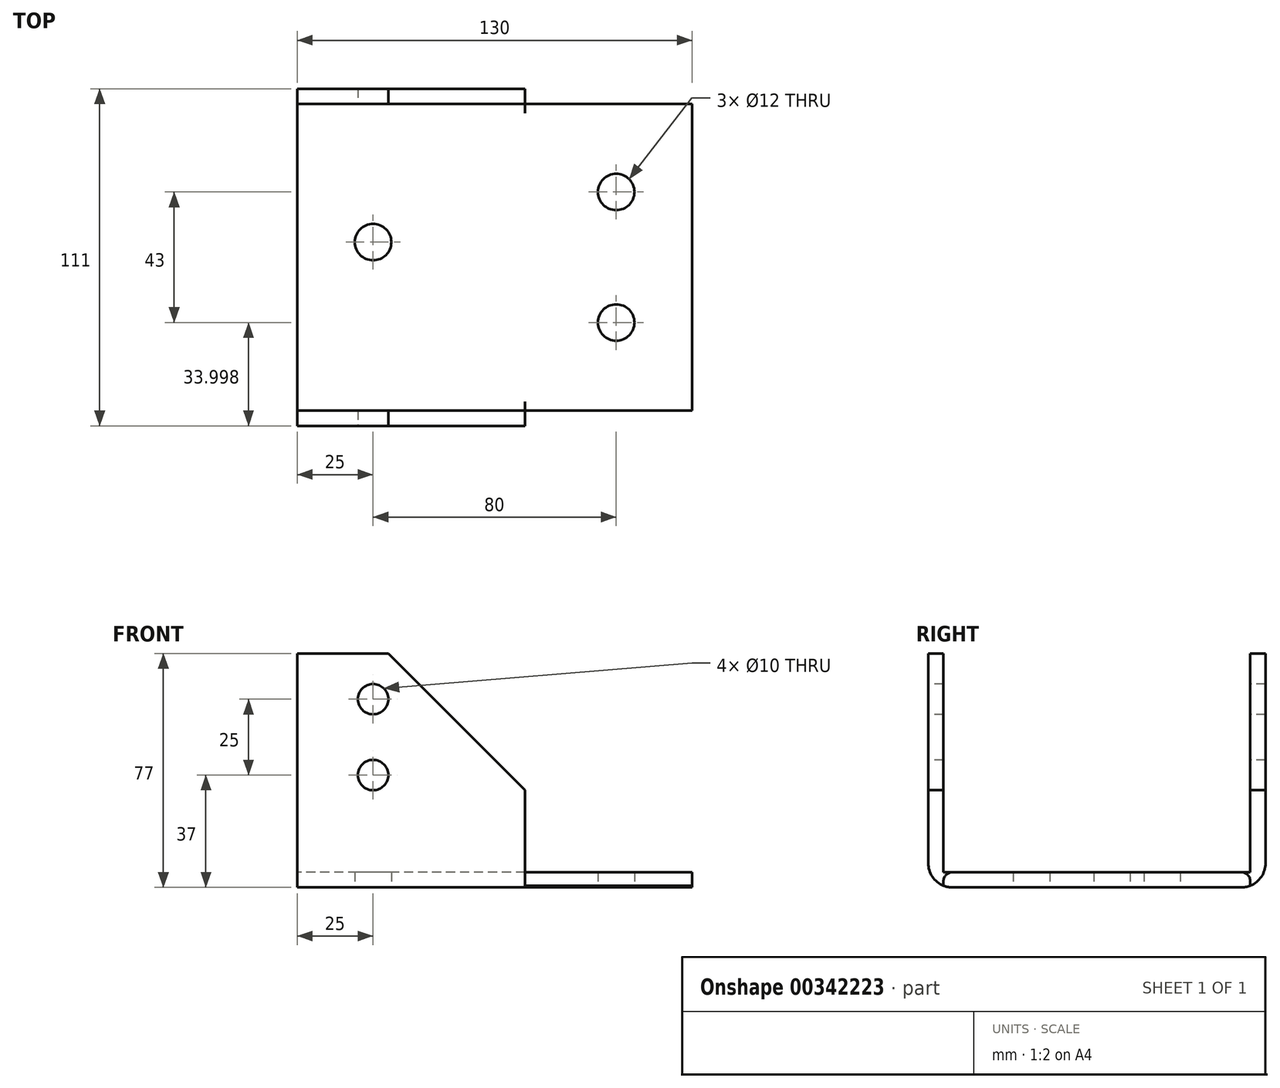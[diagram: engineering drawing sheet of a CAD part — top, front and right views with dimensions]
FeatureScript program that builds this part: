
annotation { "Feature Type Name" : "Feature", "Feature Type Description" : "" }
export const myFeature = defineFeature(function(context is Context, id is Id, definition is map)
    precondition{}
    {
        {
            var Q0;
            Q0=qCreatedBy(makeId("Top.planeOp"),FACE);
            var sketch = newSketch(context, id + "F0", { "sketchPlane" : qUnion([Q0])});
            skLineSegment(sketch, "E0", {"start": v(55, 23.64) * mm, "end": v(55, 124.64) * mm});
            skLineSegment(sketch, "E1", {"start": v(55, 124.64) * mm, "end": v(-75, 124.64) * mm});
            skLineSegment(sketch, "E2", {"start": v(-75, 124.64) * mm, "end": v(-75, 23.64) * mm});
            skLineSegment(sketch, "E3", {"start": v(-75, 23.64) * mm, "end": v(55, 23.64) * mm});
            skLineSegment(sketch, "E4", {"start": v(55, 23.64) * mm, "end": v(30, 23.64) * mm});
            skLineSegment(sketch, "E5", {"start": v(30, 23.64) * mm, "end": v(30, 52.64) * mm});
            skLineSegment(sketch, "E6", {"start": v(30, 23.64) * mm, "end": v(30, 95.64) * mm});
            skCircle(sketch, "E7", {"center": v(30, 95.64) * mm, "radius": 6 * mm});
            skCircle(sketch, "E8", {"center": v(30, 52.64) * mm, "radius": 6 * mm});
            skLineSegment(sketch, "E9", {"start": v(-75, 23.64) * mm, "end": v(-75, 79.14) * mm});
            skLineSegment(sketch, "E10", {"start": v(-75, 79.14) * mm, "end": v(-50, 79.14) * mm});
            skCircle(sketch, "E11", {"center": v(-50, 79.14) * mm, "radius": 6 * mm});
            skLineSegment(sketch, "E12", {"start": v(-75, 124.64) * mm, "end": v(-75, 129.64) * mm});
            skLineSegment(sketch, "E13", {"start": v(-75, 129.64) * mm, "end": v(0, 129.64) * mm});
            skLineSegment(sketch, "E14", {"start": v(0, 129.64) * mm, "end": v(0, 124.64) * mm});
            skLineSegment(sketch, "E15", {"start": v(-75, 23.64) * mm, "end": v(-75, 18.64) * mm});
            skLineSegment(sketch, "E16", {"start": v(-75, 18.64) * mm, "end": v(0, 18.64) * mm});
            skLineSegment(sketch, "E17", {"start": v(0, 18.64) * mm, "end": v(0, 23.64) * mm});
            skSolve(sketch);
        }
        {
            var Q0;
            {var subQ8=sQuery(id+"F0.wireOp",EDGE,"E0");Q0=makeQuery(id+"F0.imprint","IMPRINT",FACE,{"disambiguationData":[TD([[makeQuery(id+"F0.imprint","IMPRINT",EDGE,{"derivedFrom":subQ8}),1.0]])]});}
            extrude(context, id + "F1", {"entities" : qUnion([Q0]), "depth" : 5 * mm});
        }
        {
            var Q0;
            {var subQ0=sQuery(id+"F0.wireOp",EDGE,"E12");Q0=makeQuery(id+"F0.imprint","IMPRINT",FACE,{"disambiguationData":[TD([[makeQuery(id+"F0.imprint","IMPRINT",EDGE,{"derivedFrom":subQ0}),-1.0]])]});}
            var Q1;
            {var subQ0=sQuery(id+"F0.wireOp",EDGE,"E15");Q1=makeQuery(id+"F0.imprint","IMPRINT",FACE,{"disambiguationData":[TD([[makeQuery(id+"F0.imprint","IMPRINT",EDGE,{"derivedFrom":subQ0}),1.0]])]});}
            extrude(context, id + "F2", {"entities" : qUnion([Q0, Q1]), "operationType" : NewBodyOperationType.ADD, "depth" : 77 * mm});
        }
        {
            var Q0;
            Q0=makeQuery(id+"F2.opExtrude","CAP_EDGE",EDGE,{"disambiguationData":[OSD([sQuery(id+"F0.wireOp",EDGE,"E14")])],"isStart":false});
            chamfer(context, id + "F3", {"entities" : qUnion([Q0]), "width" : 45 * mm, "tangentPropagation" : true});
        }
        {
            var Q0;
            Q0=makeQuery(id+"F2.opExtrude","CAP_EDGE",EDGE,{"disambiguationData":[OSD([sQuery(id+"F0.wireOp",EDGE,"E17")])],"isStart":false});
            chamfer(context, id + "F4", {"entities" : qUnion([Q0]), "width" : 45 * mm, "tangentPropagation" : true});
        }
        {
            var Q0;
            {var subQ0=sQuery(id+"F0.wireOp",EDGE,"E1");Q0=makeQuery(id+"F2.boolean.opBoolean","SPLIT",EDGE,{"disambiguationData":[topologyDisambiguationEdgeConnected([makeQuery(id+"F2.opExtrude","SWEPT_FACE",FACE,{"disambiguationData":[OSD([subQ0])]})])],"derivedFrom":makeQuery(id+"F1.opExtrude","CAP_EDGE",EDGE,{"disambiguationData":[OSD([subQ0])],"isStart":false})});}
            var Q1;
            {var subQ0=sQuery(id+"F0.wireOp",EDGE,"E4");var subQ1=sQuery(id+"F0.wireOp",EDGE,"E3");Q1=makeQuery(id+"F2.boolean.opBoolean","SPLIT",EDGE,{"disambiguationData":[topologyDisambiguationEdgeConnected([makeQuery(id+"F2.opExtrude","SWEPT_FACE",FACE,{"disambiguationData":[OSD([subQ1])]})])],"derivedFrom":makeQuery(id+"F1.opExtrude","CAP_EDGE",EDGE,{"disambiguationData":[OSD([subQ1,subQ0])],"isStart":false})});}
            fillet(context, id + "F5", {"entities" : qUnion([Q0, Q1]), "radius" : 3 * mm, "tangentPropagation" : true, "allowEdgeOverflow" : false});
        }
        {
            var Q0;
            Q0=makeQuery(id+"F2.opExtrude","CAP_EDGE",EDGE,{"disambiguationData":[OSD([sQuery(id+"F0.wireOp",EDGE,"E16")])],"isStart":true});
            var Q1;
            Q1=makeQuery(id+"F2.opExtrude","CAP_EDGE",EDGE,{"disambiguationData":[OSD([sQuery(id+"F0.wireOp",EDGE,"E13")])],"isStart":true});
            fillet(context, id + "F6", {"entities" : qUnion([Q0, Q1]), "radius" : 8 * mm, "tangentPropagation" : true, "allowEdgeOverflow" : false});
        }
        {
            var Q0;
            Q0=makeQuery(id+"F2.opExtrude","SWEPT_FACE",FACE,{"disambiguationData":[OSD([sQuery(id+"F0.wireOp",EDGE,"E16")])]});
            var sketch = newSketch(context, id + "F7", { "sketchPlane" : qUnion([Q0])});
            skLineSegment(sketch, "E18", {"start": v(-75, 77) * mm, "end": v(-75, 62) * mm});
            skLineSegment(sketch, "E19", {"start": v(-75, 62) * mm, "end": v(-50, 62) * mm});
            skLineSegment(sketch, "E20", {"start": v(-50, 62) * mm, "end": v(-50, 37) * mm});
            skCircle(sketch, "E21", {"center": v(-50, 62) * mm, "radius": 5 * mm});
            skCircle(sketch, "E22", {"center": v(-50, 37) * mm, "radius": 5 * mm});
            skSolve(sketch);
        }
        {
            var Q0;
            Q0=sQuery(id+"F7.wireOp",VERTEX,"E22.center");
            var Q1;
            Q1=makeQuery(id+"F1.opExtrude","SWEPT_BODY",BODY,{"disambiguationData":[OSD([sQuery(id+"F0.wireOp",EDGE,"E0"),sQuery(id+"F0.wireOp",EDGE,"E1"),sQuery(id+"F0.wireOp",EDGE,"E2"),sQuery(id+"F0.wireOp",EDGE,"E3"),sQuery(id+"F0.wireOp",EDGE,"E4"),sQuery(id+"F0.wireOp",EDGE,"E7"),sQuery(id+"F0.wireOp",EDGE,"E8"),sQuery(id+"F0.wireOp",EDGE,"E9"),sQuery(id+"F0.wireOp",EDGE,"E11")])]});
            hole(context, id + "F8", {"style" : HoleStyle.SIMPLE, "endStyle" : HoleEndStyle.THROUGH, "holeDiameter" : 10 * mm, "isTappedThrough" : true, "tappedDepth" : 12 * mm, "tapClearance" : 3, "startFromSketch" : true, "locations" : qUnion([Q0]), "scope" : qUnion([Q1])});
        }
        {
            var Q0;
            Q0=sQuery(id+"F7.wireOp",VERTEX,"E21.center");
            var Q1;
            Q1=makeQuery(id+"F1.opExtrude","SWEPT_BODY",BODY,{"disambiguationData":[OSD([sQuery(id+"F0.wireOp",EDGE,"E0"),sQuery(id+"F0.wireOp",EDGE,"E1"),sQuery(id+"F0.wireOp",EDGE,"E2"),sQuery(id+"F0.wireOp",EDGE,"E3"),sQuery(id+"F0.wireOp",EDGE,"E4"),sQuery(id+"F0.wireOp",EDGE,"E7"),sQuery(id+"F0.wireOp",EDGE,"E8"),sQuery(id+"F0.wireOp",EDGE,"E9"),sQuery(id+"F0.wireOp",EDGE,"E11")])]});
            hole(context, id + "F9", {"style" : HoleStyle.SIMPLE, "endStyle" : HoleEndStyle.THROUGH, "holeDiameter" : 10 * mm, "isTappedThrough" : true, "tappedDepth" : 12 * mm, "tapClearance" : 3, "startFromSketch" : true, "locations" : qUnion([Q0]), "scope" : qUnion([Q1])});
        }
    });
